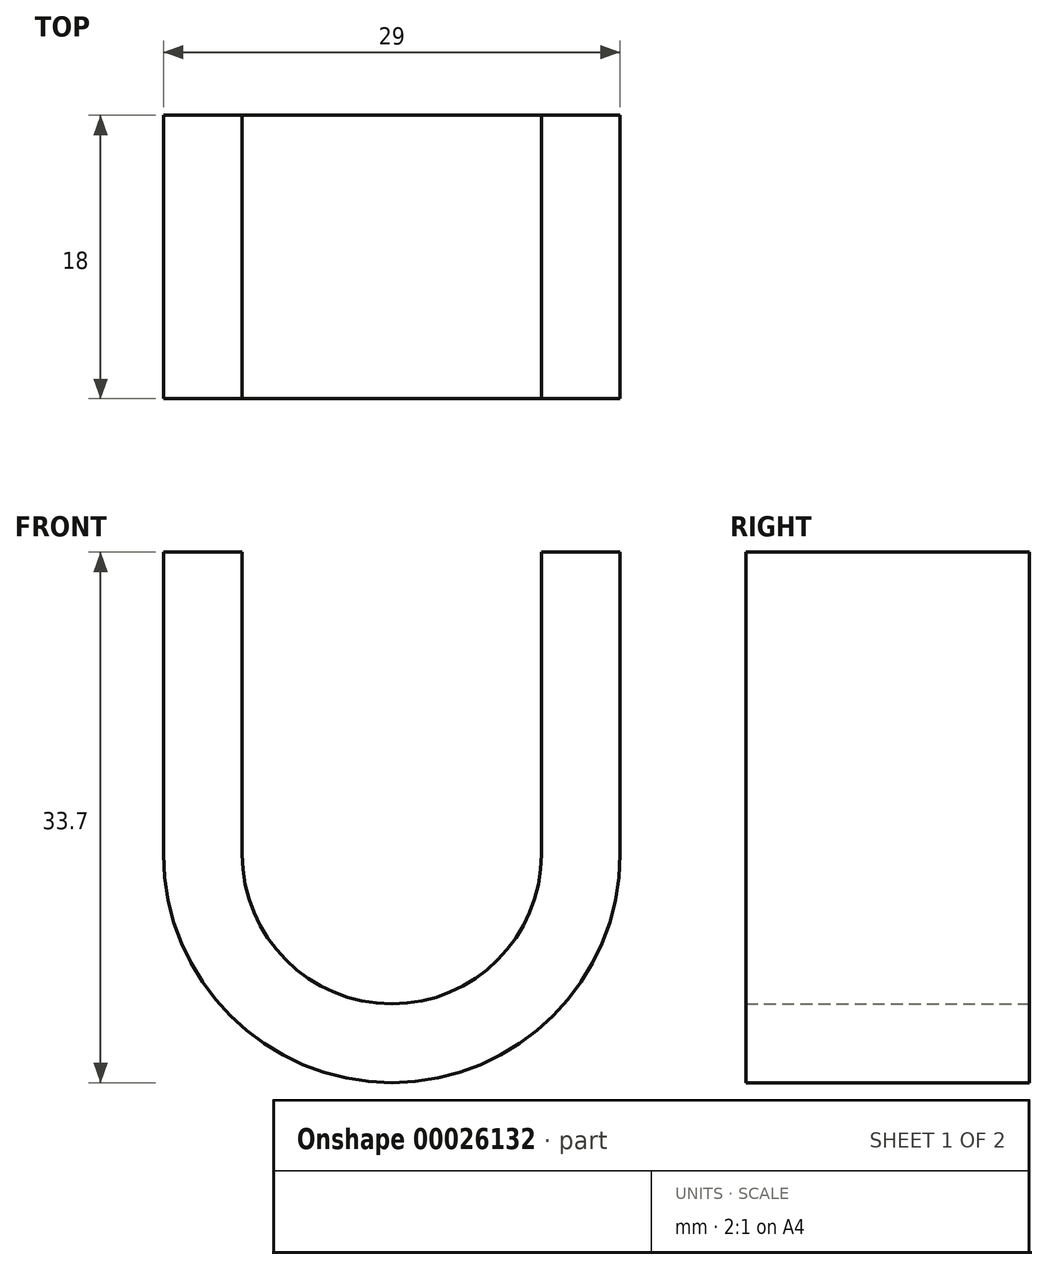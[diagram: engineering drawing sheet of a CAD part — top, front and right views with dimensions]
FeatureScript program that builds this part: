
annotation { "Feature Type Name" : "Feature", "Feature Type Description" : "" }
export const myFeature = defineFeature(function(context is Context, id is Id, definition is map)
    precondition{}
    {
        {
            var Q0;
            Q0=qCreatedBy(makeId("Front.planeOp"),FACE);
            var sketch = newSketch(context, id + "F0", { "sketchPlane" : qUnion([Q0])});
            skLineSegment(sketch, "E0.rect.top", {"start": v(14.5, 27.15) * mm, "end": v(9.5, 27.15) * mm});
            skPoint(sketch, "E0.rect.middle", {"position": v(0, 0) * mm});
            skLineSegment(sketch, "E1", {"start": v(-28.83, 17.45) * mm, "end": v(28.83, 17.45) * mm, "construction": true});
            skArc(sketch, "E2", {"start": v(-9.5, 7.95) * mm, "mid": v(0, -1.55) * mm, "end": v(9.5, 7.95) * mm});
            skLineSegment(sketch, "E3", {"start": v(-9.5, 7.95) * mm, "end": v(-9.5, 27.15) * mm});
            skLineSegment(sketch, "E4", {"start": v(9.5, 7.95) * mm, "end": v(9.5, 27.15) * mm});
            skLineSegment(sketch, "E5.trimOffspring", {"start": v(-9.5, 27.15) * mm, "end": v(-14.5, 27.15) * mm});
            skLineSegment(sketch, "E6.0", {"start": v(14.5, 7.95) * mm, "end": v(14.5, 27.15) * mm});
            skArc(sketch, "E6.1", {"start": v(-14.5, 7.95) * mm, "mid": v(0, -6.55) * mm, "end": v(14.5, 7.95) * mm});
            skLineSegment(sketch, "E6.2", {"start": v(-14.5, 7.95) * mm, "end": v(-14.5, 27.15) * mm});
            skPoint(sketch, "E0.rect.left.end.orphan", {"position": v(28.83, 27.15) * mm});
            skPoint(sketch, "E0.rect.bottom.start.orphan", {"position": v(28.83, -27.15) * mm});
            skPoint(sketch, "E7.orphan", {"position": v(-28.83, -27.15) * mm});
            skPoint(sketch, "E8.orphan", {"position": v(-28.83, 27.15) * mm});
            skSolve(sketch);
        }
        {
            var Q0;
            Q0=makeQuery(id+"F0.imprint","IMPRINT",FACE,{"disambiguationData":[TD([[makeQuery(id+"F0.imprint","IMPRINT",EDGE,{"derivedFrom":sQuery(id+"F0.wireOp",EDGE,"E0.rect.top")}),1.0]])]});
            extrude(context, id + "F1", {"entities" : qUnion([Q0]), "depth" : 18 * mm});
        }
    });
